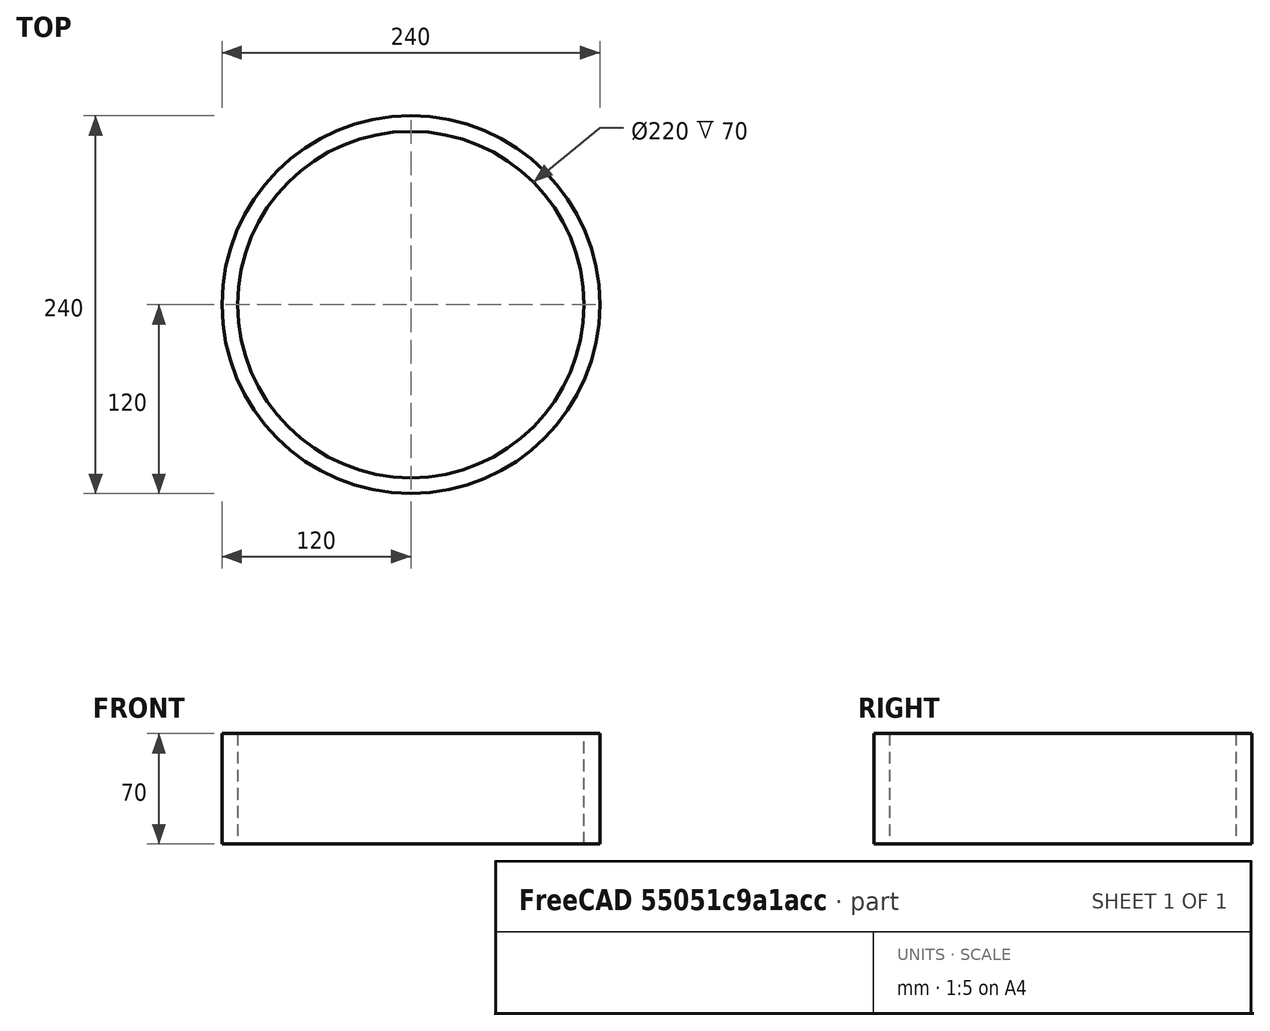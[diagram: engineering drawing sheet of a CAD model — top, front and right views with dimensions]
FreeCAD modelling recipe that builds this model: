
FCSTD DOCUMENT  (FreeCAD 2023.521R14555 (Git shallow))
Label: Base
License: All rights reserved
LicenseURL: https://en.wikipedia.org/wiki/All_rights_reserved
objects: Sketcher::SketchObject×1, PartDesign::Pad×1, PartDesign::Body×1
note: 6 computed .brp shape members not serialized (recipe doc carries the construction recipe); baked Part::Feature solids carry a one-line shape summary decoded from their .brp

FEATURE [Sketcher::SketchObject] Sketch
  ArcFitTolerance = 1e-06
  AttachmentSupport = -> [XY_Plane]
  ExternalBSplineMaxDegree = 5
  ExternalBSplineTolerance = 0.0001
  FixShape = 1
  FullyConstrained = true
  InternalTolerance = 1e-06
  InvalidShape = false
  MakeInternals = false
  MapMode = 5
  Support = -> [XY_Plane]
  TreeRank = 11
  ValidateShape = false
  sketch-geometry (2):
    g0: Circle CenterX=0 CenterY=0 CenterZ=0 NormalX=0 NormalY=0 NormalZ=1 AngleXU=0 Radius=110
    g1: Circle CenterX=0 CenterY=0 CenterZ=0 NormalX=0 NormalY=0 NormalZ=1 AngleXU=0 Radius=120
  constraints (4):
    c: Coincident(g0,g-1)
    c: Coincident(g1,g0)
    c: Diameter(g0) = 220
    c: Diameter(g1) = 240
FEATURE [PartDesign::Pad] Pad
  AddSubType = 0
  AlongSketchNormal = false
  AutoTaperInnerAngle = true
  CheckUpToFaceLimits = true
  ClaimChildren = false
  Direction = (0,0,1)
  Fit = 0
  FitJoin = 0
  FixShape = 1
  InnerFit = 0
  InnerFitJoin = 0
  InvalidShape = false
  Length = 70
  Length2 = 10
  Linearize = true
  NewSolid = false
  Profile = -> Sketch
  ReferenceAxis = -> Sketch [N_Axis]
  Refine = true
  Suppress = false
  TaperInnerAngle = 0
  TaperInnerAngleRev = 0
  TreeRank = 12
  Type = 0
  ValidateShape = true
  _ProfileBasedVersion = 1
FEATURE [PartDesign::Body] Body
  AutoGroupSolids = false
  ClaimAllChildren = false
  ExportMode = 0
  FixShape = 1
  Group = -> [Sketch,Pad]
  InvalidShape = false
  Origin = -> Origin
  Tip = -> Pad
  TreeRank = 10
  ValidateShape = false
  _ExportChildren = -> [Pad]
  _GroupVersion = 1
